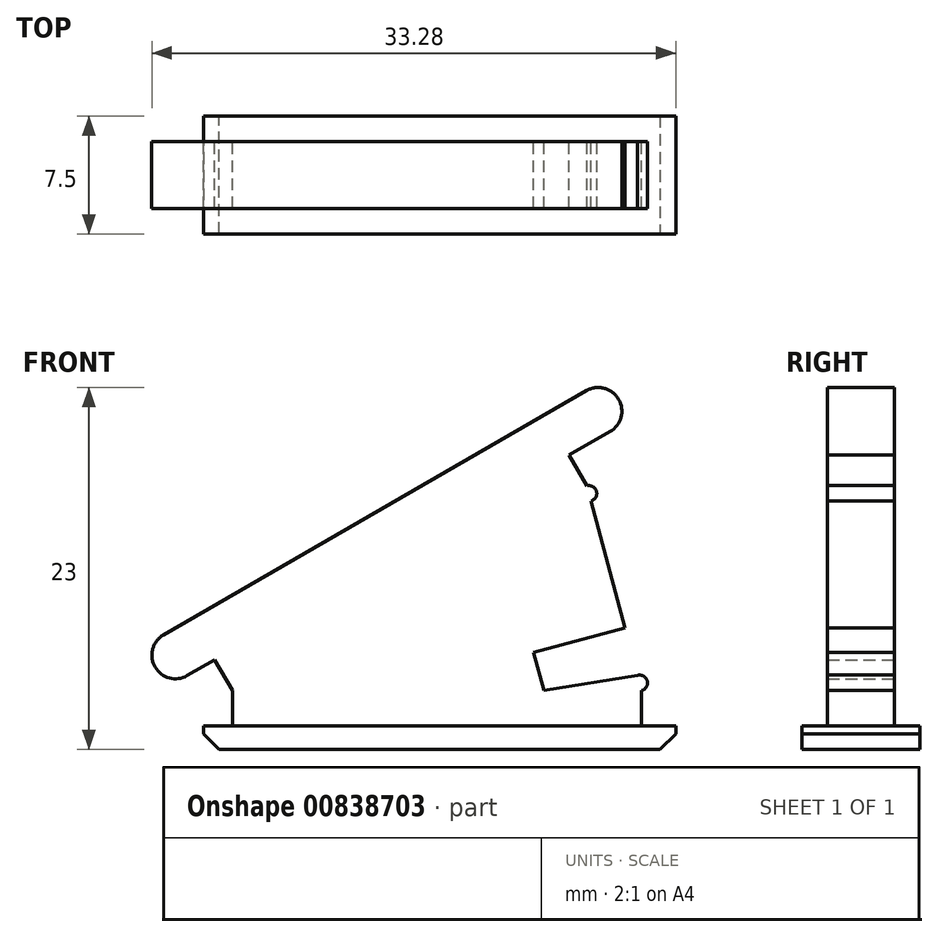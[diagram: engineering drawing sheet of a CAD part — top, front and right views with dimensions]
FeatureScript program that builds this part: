
annotation { "Feature Type Name" : "Feature", "Feature Type Description" : "" }
export const myFeature = defineFeature(function(context is Context, id is Id, definition is map)
    precondition{}
    {
        {
            var Q0;
            Q0=qCreatedBy(makeId("Front.planeOp"),FACE);
            var sketch = newSketch(context, id + "F0", { "sketchPlane" : qUnion([Q0])});
            skLineSegment(sketch, "E0.bottom", {"start": v(-24.25, 1.5) * mm, "end": v(5.75, 1.5) * mm});
            skLineSegment(sketch, "E0.top", {"start": v(-24.25, 0) * mm, "end": v(5.75, 0) * mm});
            skLineSegment(sketch, "E0.left", {"start": v(-24.25, 1.5) * mm, "end": v(-24.25, 0) * mm});
            skLineSegment(sketch, "E0.right", {"start": v(5.75, 1.5) * mm, "end": v(5.75, 0) * mm});
            skLineSegment(sketch, "E1.bottom", {"start": v(-22.42, 3.75) * mm, "end": v(3.58, 3.75) * mm});
            skLineSegment(sketch, "E1.top", {"start": v(-22.42, 1.5) * mm, "end": v(3.58, 1.5) * mm});
            skLineSegment(sketch, "E1.left", {"start": v(-22.42, 3.75) * mm, "end": v(-22.42, 1.5) * mm});
            skLineSegment(sketch, "E1.right", {"start": v(3.58, 3.75) * mm, "end": v(3.58, 1.5) * mm});
            skLineSegment(sketch, "E2.top", {"start": v(-22.42, 3.75) * mm, "end": v(0.1, 16.75) * mm});
            skLineSegment(sketch, "E2.left", {"start": v(-23.55, 5.7) * mm, "end": v(-22.42, 3.75) * mm});
            skLineSegment(sketch, "E2.right", {"start": v(-1.03, 18.7) * mm, "end": v(0.1, 16.75) * mm});
            skLineSegment(sketch, "E3", {"start": v(3.58, 3.75) * mm, "end": v(-2.63, 3.75) * mm});
            skLineSegment(sketch, "E4", {"start": v(-2.63, 3.75) * mm, "end": v(-3.28, 6.16) * mm});
            skLineSegment(sketch, "E5", {"start": v(-3.28, 6.16) * mm, "end": v(2.52, 7.72) * mm});
            skLineSegment(sketch, "E6", {"start": v(2.12, 22.25) * mm, "end": v(2.12, 22.25) * mm});
            skPoint(sketch, "E7.visualSharp", {"position": v(1.36, 23.56) * mm});
            skArc(sketch, "E7.filletArc", {"start": v(2.12, 22.25) * mm, "mid": v(1.2, 22.95) * mm, "end": v(0.06, 22.8) * mm});
            skPoint(sketch, "E8.visualSharp", {"position": v(2.86, 20.96) * mm});
            skArc(sketch, "E8.filletArc", {"start": v(1.57, 20.2) * mm, "mid": v(2.27, 21.1) * mm, "end": v(2.12, 22.25) * mm});
            skPoint(sketch, "E9.visualSharp", {"position": v(-28.08, 6.55) * mm});
            skPoint(sketch, "E10.visualSharp", {"position": v(-26.58, 3.95) * mm});
            skLineSegment(sketch, "E11", {"start": v(-1.03, 18.7) * mm, "end": v(1.57, 20.2) * mm});
            skLineSegment(sketch, "E12", {"start": v(0.1, 16.75) * mm, "end": v(2.52, 7.72) * mm});
            skArc(sketch, "E13", {"start": v(0.36, 15.78) * mm, "mid": v(0.7, 16.4) * mm, "end": v(0.1, 16.75) * mm});
            skLineSegment(sketch, "E14", {"start": v(0.06, 22.8) * mm, "end": v(-26.78, 7.3) * mm});
            skLineSegment(sketch, "E15", {"start": v(-27.33, 5.24) * mm, "end": v(-27.33, 5.24) * mm});
            skLineSegment(sketch, "E16", {"start": v(-23.55, 5.7) * mm, "end": v(-25.28, 4.7) * mm});
            skArc(sketch, "E17.filletArc", {"start": v(-26.78, 7.3) * mm, "mid": v(-27.48, 6.38) * mm, "end": v(-27.33, 5.24) * mm});
            skArc(sketch, "E18.filletArc", {"start": v(-27.33, 5.24) * mm, "mid": v(-26.42, 4.55) * mm, "end": v(-25.28, 4.7) * mm});
            skArc(sketch, "E19", {"start": v(3.58, 3.75) * mm, "mid": v(3.93, 4.36) * mm, "end": v(3.32, 4.72) * mm});
            skLineSegment(sketch, "E20", {"start": v(-2.63, 3.75) * mm, "end": v(3.32, 4.72) * mm});
            skLineSegment(sketch, "E21", {"start": v(3.32, 4.72) * mm, "end": v(3.58, 3.75) * mm});
            skSolve(sketch);
        }
        {
            var Q0;
            Q0=makeQuery(id+"F0.imprint","IMPRINT",FACE,{"disambiguationData":[TD([[makeQuery(id+"F0.imprint","IMPRINT",EDGE,{"derivedFrom":sQuery(id+"F0.wireOp",EDGE,"E0.top")}),1.0]])]});
            extrude(context, id + "F1", {"entities" : qUnion([Q0]), "endBound" : BoundingType.SYMMETRIC, "depth" : 7.5 * mm, "offsetDistance" : 25 * mm});
        }
        {
            var Q0;
            Q0=makeQuery(id+"F0.imprint","IMPRINT",FACE,{"disambiguationData":[TD([[makeQuery(id+"F0.imprint","IMPRINT",EDGE,{"derivedFrom":sQuery(id+"F0.wireOp",EDGE,"E2.top")}),1.0]])]});
            var Q1;
            {var subQ0=sQuery(id+"F0.wireOp",EDGE,"E2.right");var subQ3=sQuery(id+"F0.wireOp",EDGE,"U1OiJSbQ-nyhu-hXVJ-kdmH-V67f48ytrlkA");var subQ5=makeQuery(id+"F0.imprint","INTERSECT",VERTEX,{"derivedFrom":[subQ0,subQ3]});Q1=makeQuery(id+"F0.imprint","IMPRINT",FACE,{"disambiguationData":[TD([[makeQuery(id+"F0.imprint","IMPRINT",EDGE,{"disambiguationData":[TD([[subQ5,-1.0]])],"derivedFrom":subQ3}),1.0]])]});}
            var Q2;
            {var subQ1=sQuery(id+"F0.wireOp",EDGE,"E2.right");var subQ3=sQuery(id+"F0.wireOp",EDGE,"U1OiJSbQ-nyhu-hXVJ-kdmH-V67f48ytrlkA");var subQ4=makeQuery(id+"F0.imprint","INTERSECT",VERTEX,{"derivedFrom":[subQ1,subQ3]});Q2=makeQuery(id+"F0.imprint","IMPRINT",FACE,{"disambiguationData":[TD([[makeQuery(id+"F0.imprint","IMPRINT",EDGE,{"disambiguationData":[TD([[subQ4,1.0]])],"derivedFrom":subQ3}),1.0]])]});}
            var Q3;
            {var subQ0=sQuery(id+"F0.wireOp",EDGE,"E12");var subQ3=sQuery(id+"F0.wireOp",EDGE,"U1OiJSbQ-nyhu-hXVJ-kdmH-V67f48ytrlkA");var subQ5=makeQuery(id+"F0.imprint","INTERSECT",VERTEX,{"derivedFrom":[subQ3,subQ0]});Q3=makeQuery(id+"F0.imprint","IMPRINT",FACE,{"disambiguationData":[TD([[makeQuery(id+"F0.imprint","IMPRINT",EDGE,{"disambiguationData":[TD([[subQ5,1.0]])],"derivedFrom":subQ3}),1.0]])]});}
            var Q4;
            {var subQ2=sQuery(id+"F0.wireOp",EDGE,"E2.top");Q4=makeQuery(id+"F0.imprint","IMPRINT",FACE,{"disambiguationData":[TD([[makeQuery(id+"F0.imprint","IMPRINT",EDGE,{"derivedFrom":subQ2}),-1.0]])]});}
            var Q5;
            {var subQ0=sQuery(id+"F0.wireOp",EDGE,"E1.left");Q5=makeQuery(id+"F0.imprint","IMPRINT",FACE,{"disambiguationData":[TD([[makeQuery(id+"F0.imprint","IMPRINT",EDGE,{"derivedFrom":subQ0}),1.0]])]});}
            var Q6;
            {var subQ0=sQuery(id+"F0.wireOp",EDGE,"E3");var subQ1=sQuery(id+"F0.wireOp",EDGE,"E1.right");var subQ2=makeQuery(id+"F0.imprint","INTERSECT",VERTEX,{"derivedFrom":[subQ1,subQ0]});Q6=makeQuery(id+"F0.imprint","IMPRINT",FACE,{"disambiguationData":[TD([[makeQuery(id+"F0.imprint","IMPRINT",EDGE,{"disambiguationData":[TD([[subQ2,-1.0]])],"derivedFrom":subQ1}),1.0]])]});}
            var Q7;
            {var subQ0=sQuery(id+"F0.wireOp",EDGE,"E1.left");Q7=makeQuery(id+"F0.imprint","IMPRINT",FACE,{"disambiguationData":[TD([[makeQuery(id+"F0.imprint","IMPRINT",EDGE,{"derivedFrom":subQ0}),1.0]])]});}
            var Q8;
            {var subQ2=sQuery(id+"F0.wireOp",EDGE,"E20");Q8=makeQuery(id+"F0.imprint","IMPRINT",FACE,{"disambiguationData":[TD([[makeQuery(id+"F0.imprint","IMPRINT",EDGE,{"derivedFrom":subQ2}),-1.0]])]});}
            var Q9;
            Q9=makeQuery(id+"F0.imprint","IMPRINT",FACE,{"disambiguationData":[TD([[makeQuery(id+"F0.imprint","IMPRINT",EDGE,{"derivedFrom":sQuery(id+"F0.wireOp",EDGE,"E19")}),1.0]])]});
            var Q10;
            {var subQ0=sQuery(id+"F0.wireOp",EDGE,"E13");Q10=makeQuery(id+"F0.imprint","IMPRINT",FACE,{"disambiguationData":[TD([[makeQuery(id+"F0.imprint","IMPRINT",EDGE,{"derivedFrom":subQ0}),1.0]])]});}
            extrude(context, id + "F2", {"entities" : qUnion([Q0, Q1, Q2, Q3, Q4, Q5, Q6, Q7, Q8, Q9, Q10]), "operationType" : NewBodyOperationType.ADD, "endBound" : BoundingType.SYMMETRIC, "depth" : 4.25 * mm, "offsetDistance" : 25 * mm});
        }
        {
            var Q0;
            Q0=makeQuery(id+"F1.opExtrude","SWEPT_EDGE",EDGE,{"disambiguationData":[OSD([sQuery(id+"F0.wireOp",EDGE,"E0.top"),sQuery(id+"F0.wireOp",EDGE,"E0.left")])]});
            var Q1;
            Q1=makeQuery(id+"F1.opExtrude","SWEPT_EDGE",EDGE,{"disambiguationData":[OSD([sQuery(id+"F0.wireOp",EDGE,"E0.top"),sQuery(id+"F0.wireOp",EDGE,"E0.right")])]});
            chamfer(context, id + "F3", {"entities" : qUnion([Q0, Q1]), "width" : 1 * mm, "tangentPropagation" : true});
        }
    });
